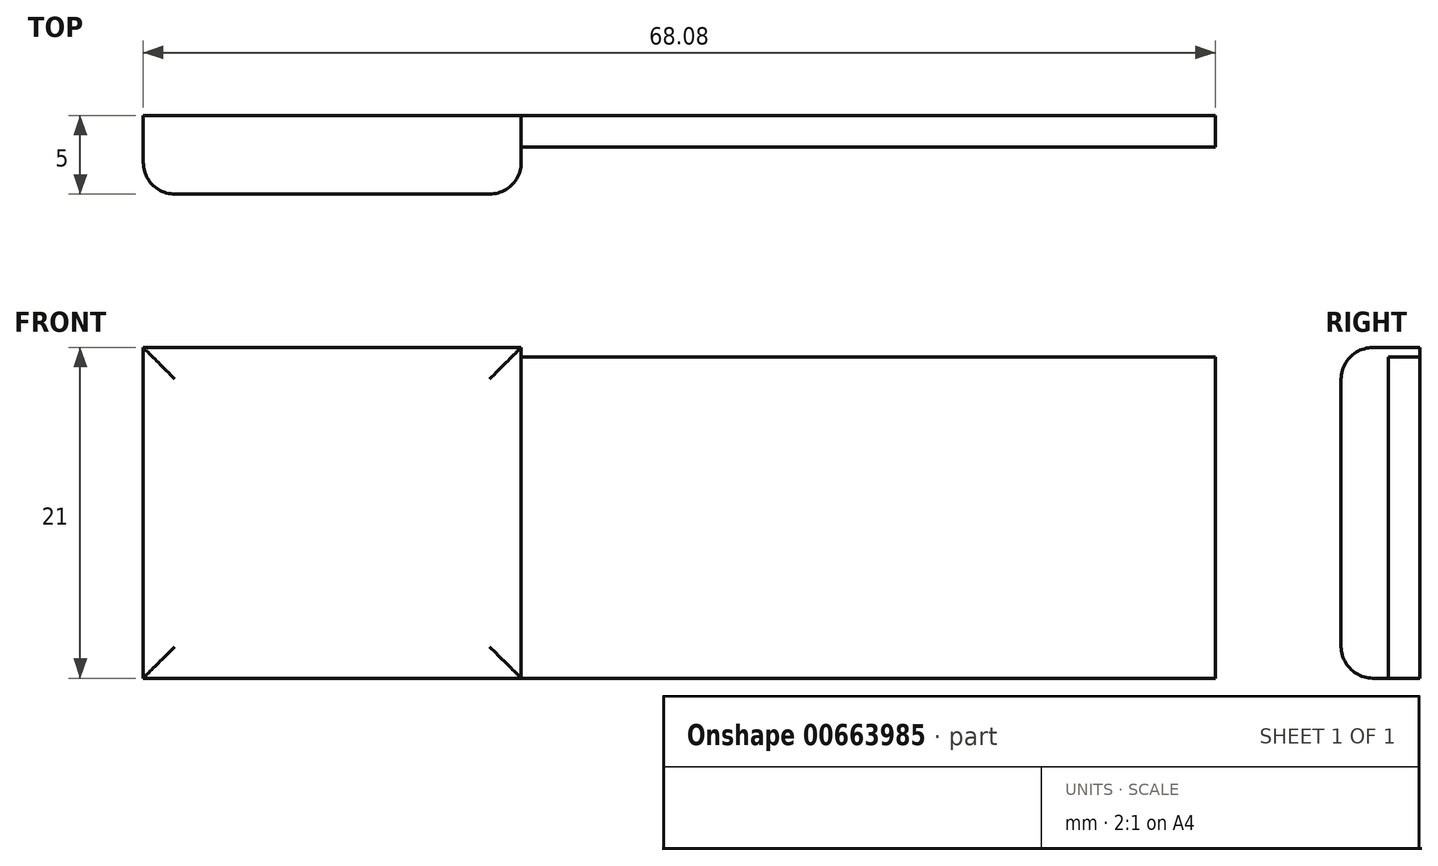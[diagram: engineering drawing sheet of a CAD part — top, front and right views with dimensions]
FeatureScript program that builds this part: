
annotation { "Feature Type Name" : "Feature", "Feature Type Description" : "" }
export const myFeature = defineFeature(function(context is Context, id is Id, definition is map)
    precondition{}
    {
        {
            var Q0;
            Q0=qCreatedBy(makeId("Front.planeOp"),FACE);
            var sketch = newSketch(context, id + "F0", { "sketchPlane" : qUnion([Q0])});
            skLineSegment(sketch, "E0.bottom", {"start": v(0, 0) * mm, "end": v(-24, 0) * mm});
            skLineSegment(sketch, "E0.top", {"start": v(0, 21) * mm, "end": v(-24, 21) * mm});
            skLineSegment(sketch, "E0.left", {"start": v(0, 0) * mm, "end": v(0, 21) * mm});
            skLineSegment(sketch, "E0.right", {"start": v(-24, 0) * mm, "end": v(-24, 21) * mm});
            skSolve(sketch);
        }
        {
            var Q0;
            Q0 = qSketchRegion(id + "F0", true);
            extrude(context, id + "F1", {"entities" : qUnion([Q0]), "depth" : 5 * mm, "offsetDistance" : 25 * mm});
        }
        {
            var Q0;
            Q0=makeQuery(id+"F1.opExtrude","CAP_FACE",FACE,{"disambiguationData":[OSD([sQuery(id+"F0.wireOp",EDGE,"E0.bottom"),sQuery(id+"F0.wireOp",EDGE,"E0.top"),sQuery(id+"F0.wireOp",EDGE,"E0.left"),sQuery(id+"F0.wireOp",EDGE,"E0.right")])],"isStart":false});
            fillet(context, id + "F2", {"entities" : qUnion([Q0]), "radius" : 2 * mm, "tangentPropagation" : true, "allowEdgeOverflow" : false});
        }
        {
            var Q0;
            Q0=qCreatedBy(makeId("Front.planeOp"),FACE);
            var sketch = newSketch(context, id + "F3", { "sketchPlane" : qUnion([Q0])});
            skLineSegment(sketch, "E1.bottom", {"start": v(0, 0) * mm, "end": v(44.08, 0) * mm});
            skLineSegment(sketch, "E1.top", {"start": v(0, 20.4) * mm, "end": v(44.08, 20.4) * mm});
            skLineSegment(sketch, "E1.left", {"start": v(0, 0) * mm, "end": v(0, 20.4) * mm});
            skLineSegment(sketch, "E1.right", {"start": v(44.08, 0) * mm, "end": v(44.08, 20.4) * mm});
            skSolve(sketch);
        }
        {
            var Q0;
            Q0 = qSketchRegion(id + "F3", true);
            extrude(context, id + "F4", {"entities" : qUnion([Q0]), "operationType" : NewBodyOperationType.ADD, "depth" : 2 * mm, "offsetDistance" : 25 * mm});
        }
    });
